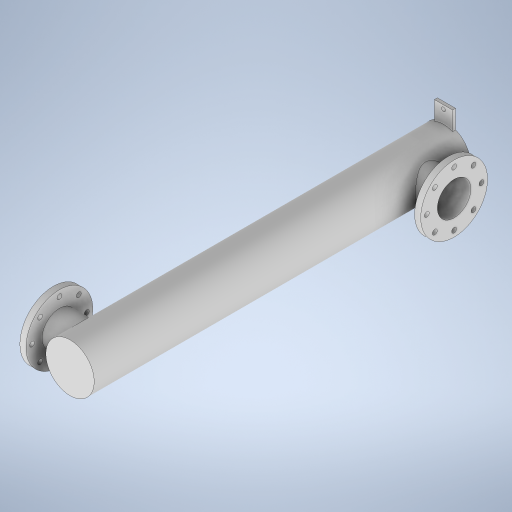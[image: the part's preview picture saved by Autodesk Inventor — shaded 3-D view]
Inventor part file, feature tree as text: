
AUTODESK INVENTOR PART (.ipt)
format: ipt  version: 2023.2 (Build 272271030, 271C)  size: 460,800 bytes
history: native  units: mm
features: extrude x6, sketch x6, projected_geometry x3, other x2, pattern_circular x1
ambient origin geometry x8: Origin, YZ Plane, XZ Plane, XY Plane, X Axis, Y Axis, Z Axis, Center Point
bodies: Solid1 (feature_tree)
feature tree (18):
  extrude  "Extrusion1"  Depth=100.0mm
  pattern_circular  "Circular Pattern1"  Count=3 Angle=360.0deg
  extrude  "Extrusion2"  Depth=1240.0mm TaperAngle=0.0deg
  extrude  "Extrusion3"  Depth=20.0mm
  extrude  "Extrusion4"  Depth=20.0mm
  extrude  "Extrusion5"  Depth=20.0mm TaperAngle=0.0deg
  extrude  "Extrusion6"  Depth=20.0mm
  sketch  "Sketch1"  dims[d9=60.0mm d10=100.0mm]
  other  "Image1"
  sketch  "Sketch2"  dims[d13=135.0mm]
  sketch  "Sketch3"  dims[d14=13.0mm]
  sketch  "Sketch4"  dims[d15=13.0mm]
  other  "Image2"
  projected_geometry  "Projected Loop1"
  sketch  "Sketch5"  dims[d16=10.0mm d17=0.0mm d18=30.0mm d19=360.0deg]
  projected_geometry  "Projected Loop2"
  sketch  "Sketch6"  dims[d21=159.0mm d22=1240.0mm d23=0.0mm d24=114.0mm d25=125.0mm d26=150.0mm d27=0.0mm d28=114.0mm d29=1145.0mm d30=150.0mm d31=0.0mm d71=180.0mm d90=89.980359mm d93=95.0mm d94=220.0mm d95=180.0mm d96=16.0mm d97=80.0mm d99=360.0deg d101=20.0mm d102=0.0mm d103=2.0mm d105=80.0mm d106=220.0mm d107=180.0mm d108=16.0mm d109=360.0deg d110=20.0mm d111=0.0mm d112=2.0mm]
  projected_geometry  "Projected Loop3"
